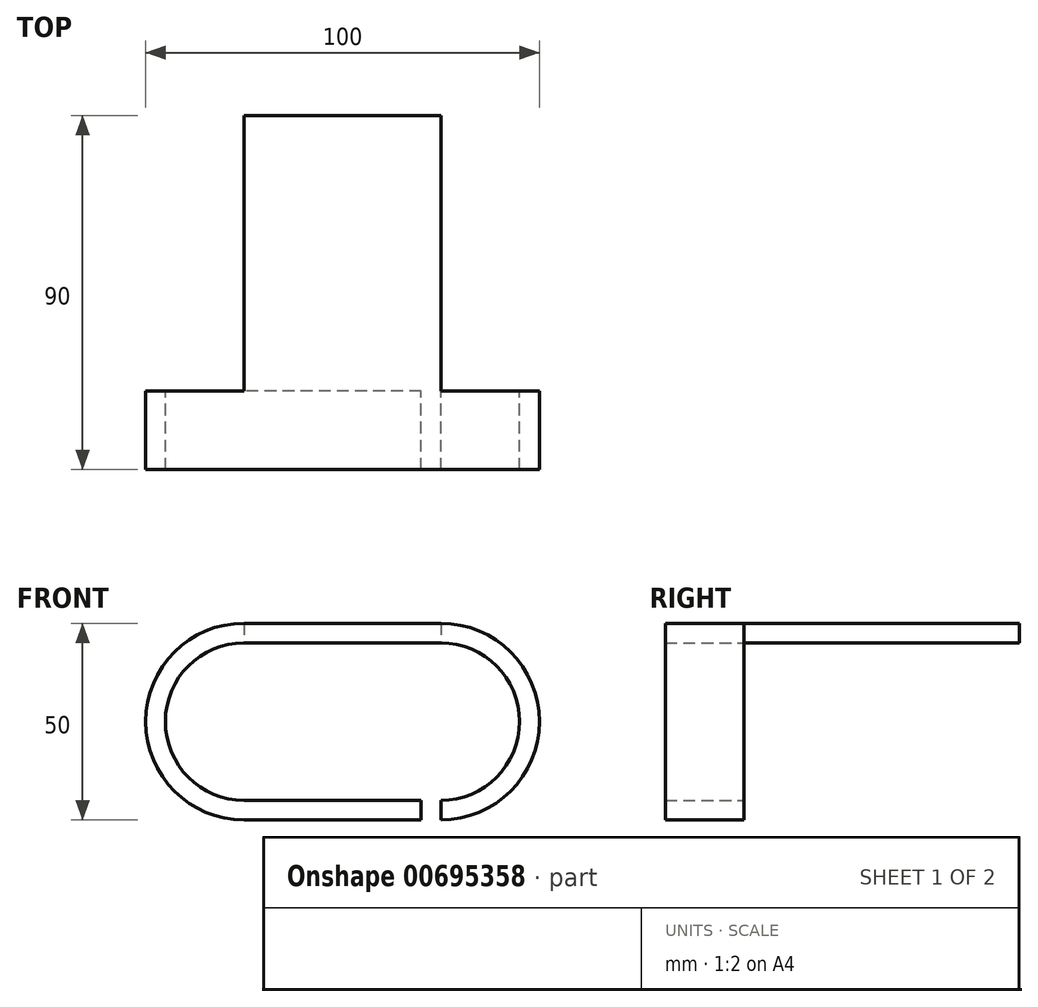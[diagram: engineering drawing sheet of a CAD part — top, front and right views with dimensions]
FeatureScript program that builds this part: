
annotation { "Feature Type Name" : "Feature", "Feature Type Description" : "" }
export const myFeature = defineFeature(function(context is Context, id is Id, definition is map)
    precondition{}
    {
        {
            var Q0;
            Q0=qCreatedBy(makeId("Front.planeOp"),FACE);
            var sketch = newSketch(context, id + "F0", { "sketchPlane" : qUnion([Q0])});
            skLineSegment(sketch, "E0", {"start": v(0, 0) * mm, "end": v(-50, 0) * mm});
            skLineSegment(sketch, "E1", {"start": v(-50, 40) * mm, "end": v(0, 40) * mm});
            skArc(sketch, "E2", {"start": v(-50, 40) * mm, "mid": v(-70, 20) * mm, "end": v(-50, 0) * mm});
            skArc(sketch, "E3", {"start": v(0, 0) * mm, "mid": v(20, 20) * mm, "end": v(0, 40) * mm});
            skLineSegment(sketch, "E4.0", {"start": v(-50, 45) * mm, "end": v(0, 45) * mm});
            skArc(sketch, "E4.1", {"start": v(-50, 45) * mm, "mid": v(-75, 20) * mm, "end": v(-50, -5) * mm});
            skLineSegment(sketch, "E4.2", {"start": v(0, -5) * mm, "end": v(-50, -5) * mm});
            skArc(sketch, "E4.3", {"start": v(0, -5) * mm, "mid": v(25, 20) * mm, "end": v(0, 45) * mm});
            skLineSegment(sketch, "E5", {"start": v(0, 0) * mm, "end": v(0, -5) * mm});
            skLineSegment(sketch, "E6", {"start": v(0, -5) * mm, "end": v(-5, -5) * mm});
            skLineSegment(sketch, "E7", {"start": v(-5, -5) * mm, "end": v(-5, 0) * mm});
            skLineSegment(sketch, "E8.bottom", {"start": v(0, 45) * mm, "end": v(-50, 45) * mm});
            skLineSegment(sketch, "E8.top", {"start": v(0, 40) * mm, "end": v(-50, 40) * mm});
            skLineSegment(sketch, "E8.left", {"start": v(0, 45) * mm, "end": v(0, 40) * mm});
            skLineSegment(sketch, "E8.right", {"start": v(-50, 45) * mm, "end": v(-50, 40) * mm});
            skSolve(sketch);
        }
        {
            var Q0;
            Q0=makeQuery(id+"F0.imprint","IMPRINT",FACE,{"disambiguationData":[TD([[makeQuery(id+"F0.imprint","IMPRINT",EDGE,{"derivedFrom":sQuery(id+"F0.wireOp",EDGE,"E3")}),-1.0]])]});
            var Q1;
            Q1=makeQuery(id+"F0.imprint","IMPRINT",FACE,{"disambiguationData":[TD([[makeQuery(id+"F0.imprint","IMPRINT",EDGE,{"derivedFrom":sQuery(id+"F0.wireOp",EDGE,"E1")}),1.0]])]});
            var Q2;
            {var subQ3=sQuery(id+"F0.wireOp",EDGE,"E2");Q2=makeQuery(id+"F0.imprint","IMPRINT",FACE,{"disambiguationData":[TD([[makeQuery(id+"F0.imprint","IMPRINT",EDGE,{"derivedFrom":subQ3}),-1.0]])]});}
            extrude(context, id + "F1", {"entities" : qUnion([Q0, Q1, Q2]), "depth" : 20 * mm, "offsetDistance" : 25 * mm});
        }
        {
            var Q0;
            Q0=makeQuery(id+"F0.imprint","IMPRINT",FACE,{"disambiguationData":[TD([[makeQuery(id+"F0.imprint","IMPRINT",EDGE,{"derivedFrom":sQuery(id+"F0.wireOp",EDGE,"E1")}),1.0]])]});
            extrude(context, id + "F2", {"entities" : qUnion([Q0]), "operationType" : NewBodyOperationType.ADD, "oppositeDirection" : true, "depth" : 70 * mm, "offsetDistance" : 25 * mm});
        }
    });
